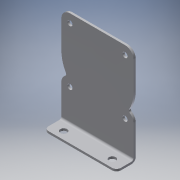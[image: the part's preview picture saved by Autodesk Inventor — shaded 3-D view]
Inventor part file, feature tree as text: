
AUTODESK INVENTOR PART (.ipt)
format: ipt  version: 2016 (Build 200138000, 138)  size: 187,904 bytes
history: native  units: in
note: dims shown in document units (in); Inventor stores cm internally (conversion verified against a paired STEP export)
features: sketch x6, extrude x4, fillet x3, hole x2, reference x2, plane x1, mirror x1
ambient origin geometry x8: Origin, YZ Plane, XZ Plane, XY Plane, X Axis, Y Axis, Z Axis, Center Point
bodies: Solid1 (feature_tree)
feature tree (19):
  extrude  "Extrusion1"  Depth=2.11in
  extrude  "Extrusion5"  Depth=2.11in
  extrude  "Extrusion2"  Depth=0.5in TaperAngle=0.0deg
  extrude  "Extrusion4"  Depth=0.25in TaperAngle=0.0deg
  hole  "Hole3"  [1 undecoded]
  plane  "Work Plane1"
  fillet  "Fillet3"  Radius=0.063in
  fillet  "Fillet4"  Radius=0.125in
  fillet  "Fillet5"  Radius=0.125in
  hole  "Hole6"  [1 undecoded]
  mirror  "Mirror1"
  sketch  "Sketch1"  dims[d0=2.11in d1=2.5in]
  sketch  "Sketch2"  dims[d2=0.0625in d3=0.0in d4=2.11in]
  sketch  "Sketch6"  dims[d6=0.5in d7=0.0in d29=1.0in d30=0.0in]
  reference  "Reference2"
  sketch  "Sketch7"  dims[d31=0.15in d32=0.75in d33=0.279in d34=0.25in d35=0.5635in d36=1.0in d37=0.8108in d57=1.0in d58=0.0in]
  sketch  "Sketch9"  dims[d59=0.063in d60=2.856in d61=0.063in d62=0.125in d63=0.125in]
  sketch  "Sketch10"  dims[d64=0.201in d65=0.75in d66=0.385in d67=0.25in d68=0.5635in d69=1.0in d70=0.8108in]
  reference  "Reference3"
note: 2 required parameter values undecoded (feature->parameter linkage not recoverable at this tier; creation-order binding heuristic only, values carry confidence <= 0.55)
